# Revit family: IS_Conca_BC754_BIM_GB
name_source: partatom
category: Plumbing Fixtures
revit_build: Autodesk Revit 2017 (Build: 20160225_1515(x64)
units: mm (PartAtom-declared; Revit-internal decimal feet)

## family parameters
Always vertical = No
Cut with Voids When Loaded = No
OmniClass Number = 23.45.55.17
OmniClass Title = Mixing Faucets
Part Type = Normal
Room Calculation Point = No
Round Connector Dimension = Use Diameter
Shared = No
Work Plane-Based = No

## types (4) — shared parameters
Accessories = https://www.idealspec.co.uk
AreaUnits = millimeters
AssetType = Fixed
BIMObjectName = IS_IdealStandard_WashbasinTaps_Conca_BC754
BIMobject category = Sanitary: Taps & Mixer
BarCode = 3800861085669
Brand = Ideal Standard
Brand url = http://www.idealstandard.co.uk
ConnectionType = Plumbing
CurrencyUnit = £
CurrentRevision = 1
Date of publishing = 22/09/2020
Description = Conca Single Lever basin mixer slim no waste - 5 litres per minute Eco flow regulator fitted.
Edition number = 1
ExpectedLife = 30
FaucetFunction = UNSET
FaucetOperation = OTHER
FaucetType = OTHER
Features = Single lever basin mixer slim no waste - 5 litres per minute Eco flow regulator fitted.
FlushRate = 0.00 m³
GTIN code = https://3800861085669
Help = https://www.idealspec.co.uk
IFC Classification = Sanitary Terminal
IfcExportAs = IfcValveType
IfcExportType = FAUCET
Installation instructions = https://www.idealspec.co.uk
InstallationInstructions = https://www.idealspec.co.uk
IsBuiltIn = No
IsHighPressure = No
IsSingleFlush = No
LinearUnits = millimeters
MaintenanceInformation = https://www.idealspec.co.uk
Manufacturer = Ideal Standard (UK) Ltd
Manufacturer name = Ideal Standard
ManufacturerURL = https://www.idealspec.co.uk
Material = Brass
Material main = Brass
ModelReference = Single lever basin mixer slim no waste - 5 litres per minute Eco flow regulator fitted.
NBS Reference Code = 45-35-70/371
NBS Reference Description = Water supply fittings for wash basins and troughs
Name = WashbasinTaps_Conca_BC754_IdealStandard
NettWeight = 1,25 KG
NominalDepth = 183 mm
NominalHeight = 97 mm
NominalLength = 183 mm
NominalWidth = 48 mm
Product Guid = dec9e631-6d31-4744-b0de-ae1d157024c9
Product SKU = BC754
Product certification = https://www.idealspec.co.uk
Product data url = https://bimobject.com
Product family = Conca
Product group = BASIN MIXER
Product name = CONCA BSN MXR R-MTD 5L NO PUW BR GUNM
Product url = https://www.idealstandard.co.uk
ProductInformation = https://www.idealspec.co.uk
QR code = http://bimobject.com
Shape = Cylindrical
Size = 48 x 183 x 97 mm
Space = Internal
SpareParts = https://fastpart-spares.co.uk
Technical description = https://www.idealspec.co.uk
TestPressure = 10 Bar
UNSPSC Code = 301815
URL = https://www.idealspec.co.uk
Uniclass 1.4 Code = L725111
Uniclass 1.4 Description = Mixer taps
Uniclass 2.0 Code = Pr_40_30_96_98
Uniclass 2.0 Description = Washbasin Taps
Uniclass 2015 Code = Pr_40_20_87_98
Uniclass 2015 Name = Washbasin taps
Uniclass2015Code = Pr_40_20_87_98
Uniclass2015Title = Washbasin taps
Uniclass2015Version = v1.1
Uniformat II Code = Pr_40_30_96_98
Uniformat II Description = Washbasin Taps
Version = 1
VolumeUnits = Litres
WRASURL = https://www.wras.co.uk
WarrantyDescription = Manufacturers Warranty
WarrantyDurationParts = 5
WarrantyDurationUnit = year
WarrantyGuarantorParts = https://www.idealspec.co.uk
zero-valued in all types: FlushingRate, InletConnectionSize, MaterialThickness, OutletConnectionSize

## per-type parameters (varying)
| type | Color | Finish | MainColor | Model | ModelNumber |
| BC754AA - CONCA BSN MXR R-MTD 5L NO PUW CHR | Chrome | Chrome | Chrome | BC754AA | BC754AA |
| BC754A2 - CONCA BSN MXR R-MTD 5L NO PUW BR GOLD | Brushed gold | Brushed gold | Brushed gold | BC754A2 | BC754A2 |
| BC754A5 - CONCA BSN MXR R-MTD 5L NO PUW MGN GREY | Brushed Gun metal | Brushed Gun metal | Brushed Gun metal | BC754A5 | BC754A5 |
| BC754GN - CONCA BSN MXR R-MTD 5L NO PUW SILV STORM | Brushed nickel | Brushed nickel | Brushed nickel | BC754GN | BC754GN |

## geometry (parser evidence)
native form markers: Sweep x2
no freeform markers — native parametric forms only
